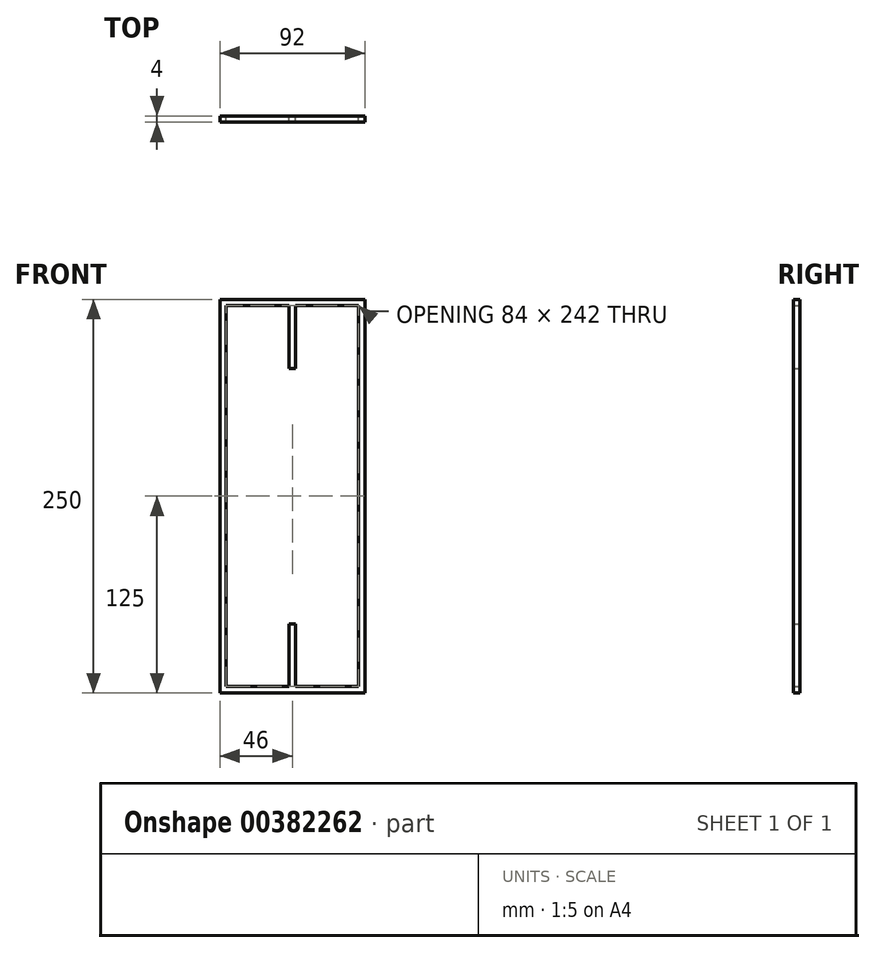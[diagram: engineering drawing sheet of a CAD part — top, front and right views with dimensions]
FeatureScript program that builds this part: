
annotation { "Feature Type Name" : "Feature", "Feature Type Description" : "" }
export const myFeature = defineFeature(function(context is Context, id is Id, definition is map)
    precondition{}
    {
        {
            var Q0;
            Q0=qCreatedBy(makeId("Front.planeOp"),FACE);
            var sketch = newSketch(context, id + "F0", { "sketchPlane" : qUnion([Q0])});
            skPoint(sketch, "E0", {"position": v(0, 0) * mm});
            skPoint(sketch, "E1", {"position": v(46, 0) * mm});
            skPoint(sketch, "E2", {"position": v(0, 125) * mm});
            skPoint(sketch, "E3", {"position": v(-95.35, 0) * mm});
            skLineSegment(sketch, "E4", {"start": v(-95.35, 0) * mm, "end": v(96.76, 0) * mm});
            skPoint(sketch, "E5.MirrorP", {"position": v(0, -125) * mm});
            skLineSegment(sketch, "E6", {"start": v(0, 125) * mm, "end": v(0, -125) * mm});
            skPoint(sketch, "E7", {"position": v(46, 125) * mm});
            skPoint(sketch, "E8.MirrorP", {"position": v(-46, 0) * mm});
            skPoint(sketch, "E9", {"position": v(-46, 125) * mm});
            skPoint(sketch, "E10", {"position": v(46, -125) * mm});
            skPoint(sketch, "E11", {"position": v(-46, -125) * mm});
            skLineSegment(sketch, "E12.bottom", {"start": v(46, 125) * mm, "end": v(42, 125) * mm});
            skLineSegment(sketch, "E12.top", {"start": v(46, -125) * mm, "end": v(42, -125) * mm});
            skLineSegment(sketch, "E12.left", {"start": v(46, 125) * mm, "end": v(46, -125) * mm});
            skLineSegment(sketch, "E12.right", {"start": v(42, 125) * mm, "end": v(42, -125) * mm});
            skLineSegment(sketch, "E13.bottom", {"start": v(-46, 125) * mm, "end": v(-42, 125) * mm});
            skLineSegment(sketch, "E13.top", {"start": v(-46, -125) * mm, "end": v(-42, -125) * mm});
            skLineSegment(sketch, "E13.left", {"start": v(-46, 125) * mm, "end": v(-46, -125) * mm});
            skLineSegment(sketch, "E13.right", {"start": v(-42, 125) * mm, "end": v(-42, -125) * mm});
            skLineSegment(sketch, "E14.bottom", {"start": v(-42, 125) * mm, "end": v(42, 125) * mm});
            skLineSegment(sketch, "E14.top", {"start": v(-42, 121) * mm, "end": v(42, 121) * mm});
            skLineSegment(sketch, "E14.left", {"start": v(-42, 125) * mm, "end": v(-42, 121) * mm});
            skLineSegment(sketch, "E14.right", {"start": v(42, 125) * mm, "end": v(42, 121) * mm});
            skLineSegment(sketch, "E15.bottom", {"start": v(-42, -125) * mm, "end": v(42, -125) * mm});
            skLineSegment(sketch, "E15.top", {"start": v(-42, -121) * mm, "end": v(42, -121) * mm});
            skLineSegment(sketch, "E15.left", {"start": v(-42, -125) * mm, "end": v(-42, -121) * mm});
            skLineSegment(sketch, "E15.right", {"start": v(42, -125) * mm, "end": v(42, -121) * mm});
            skPoint(sketch, "E16", {"position": v(-42, 81) * mm});
            skPoint(sketch, "E17", {"position": v(42, 81) * mm});
            skPoint(sketch, "E18", {"position": v(42, -81) * mm});
            skPoint(sketch, "E19", {"position": v(-42, -81) * mm});
            skPoint(sketch, "E20", {"position": v(42, -15) * mm});
            skPoint(sketch, "E21", {"position": v(-42, -15) * mm});
            skPoint(sketch, "E22", {"position": v(-42, 15) * mm});
            skPoint(sketch, "E23", {"position": v(42, 15) * mm});
            skLineSegment(sketch, "E24.bottom", {"start": v(-42, 15) * mm, "end": v(42, 15) * mm});
            skLineSegment(sketch, "E24.top", {"start": v(-42, -15) * mm, "end": v(42, -15) * mm});
            skLineSegment(sketch, "E24.left", {"start": v(-42, 15) * mm, "end": v(-42, -15) * mm});
            skLineSegment(sketch, "E24.right", {"start": v(42, 15) * mm, "end": v(42, -15) * mm});
            skLineSegment(sketch, "E25.bottom", {"start": v(-42, -81) * mm, "end": v(42, -81) * mm});
            skLineSegment(sketch, "E25.top", {"start": v(-42, -77) * mm, "end": v(42, -77) * mm});
            skLineSegment(sketch, "E25.left", {"start": v(-42, -81) * mm, "end": v(-42, -77) * mm});
            skLineSegment(sketch, "E25.right", {"start": v(42, -81) * mm, "end": v(42, -77) * mm});
            skLineSegment(sketch, "E26.bottom", {"start": v(-42, 81) * mm, "end": v(42, 81) * mm});
            skLineSegment(sketch, "E26.top", {"start": v(-42, 77) * mm, "end": v(42, 77) * mm});
            skLineSegment(sketch, "E26.left", {"start": v(-42, 81) * mm, "end": v(-42, 77) * mm});
            skLineSegment(sketch, "E26.right", {"start": v(42, 81) * mm, "end": v(42, 77) * mm});
            skLineSegment(sketch, "E27.top", {"start": v(-42, 11) * mm, "end": v(42, 11) * mm});
            skLineSegment(sketch, "E27.left", {"start": v(-42, 15) * mm, "end": v(-42, 11) * mm});
            skLineSegment(sketch, "E27.right", {"start": v(42, 15) * mm, "end": v(42, 11) * mm});
            skLineSegment(sketch, "E28.top", {"start": v(-42, -11) * mm, "end": v(42, -11) * mm});
            skLineSegment(sketch, "E28.left", {"start": v(-42, -15) * mm, "end": v(-42, -11) * mm});
            skLineSegment(sketch, "E28.right", {"start": v(42, -15) * mm, "end": v(42, -11) * mm});
            skPoint(sketch, "E29", {"position": v(-42, -89) * mm});
            skPoint(sketch, "E30", {"position": v(-2, -81) * mm});
            skPoint(sketch, "E31", {"position": v(0, -81) * mm});
            skPoint(sketch, "E32.MirrorP", {"position": v(2, -81) * mm});
            skLineSegment(sketch, "E33", {"start": v(-2, -81) * mm, "end": v(-2, -121) * mm});
            skLineSegment(sketch, "E34.MirrorCS", {"start": v(2, -81) * mm, "end": v(2, -121) * mm});
            skPoint(sketch, "E35", {"position": v(-2, -113) * mm});
            skLineSegment(sketch, "E36", {"start": v(-42, -89) * mm, "end": v(-22, -89) * mm});
            skLineSegment(sketch, "E37", {"start": v(-2, -113) * mm, "end": v(-22, -113) * mm});
            skLineSegment(sketch, "E38", {"start": v(-22, -89) * mm, "end": v(-2, -113) * mm});
            skLineSegment(sketch, "E39", {"start": v(-42, -89) * mm, "end": v(-22, -113) * mm});
            skPoint(sketch, "E40", {"position": v(-22, -92.12) * mm});
            skPoint(sketch, "E41", {"position": v(-36.24, -92.78) * mm});
            skPoint(sketch, "E42", {"position": v(-2, 121) * mm});
            skLineSegment(sketch, "E43", {"start": v(-2, 121) * mm, "end": v(-2, 81) * mm});
            skLineSegment(sketch, "E44.MirrorCS", {"start": v(2, 121) * mm, "end": v(2, 81) * mm});
            skPoint(sketch, "E45", {"position": v(0, -15) * mm});
            skPoint(sketch, "E46", {"position": v(0, 15) * mm});
            skLineSegment(sketch, "E47", {"start": v(-42, 77) * mm, "end": v(42, 15) * mm});
            skLineSegment(sketch, "E48", {"start": v(-42, 15) * mm, "end": v(42, 77) * mm});
            skLineSegment(sketch, "E49.bottom", {"start": v(-32.6, 70.06) * mm, "end": v(32.6, 70.06) * mm});
            skLineSegment(sketch, "E49.top", {"start": v(-32.6, 21.94) * mm, "end": v(32.6, 21.94) * mm});
            skLineSegment(sketch, "E49.left", {"start": v(-32.6, 70.06) * mm, "end": v(-32.6, 21.94) * mm});
            skLineSegment(sketch, "E49.right", {"start": v(32.6, 70.06) * mm, "end": v(32.6, 21.94) * mm});
            skPoint(sketch, "E49.middle", {"position": v(0, 46) * mm});
            skLineSegment(sketch, "E50", {"start": v(-42, -15) * mm, "end": v(42, -77) * mm});
            skLineSegment(sketch, "E51", {"start": v(-42, -77) * mm, "end": v(42, -15) * mm});
            skLineSegment(sketch, "E52.bottom", {"start": v(32.5, -22.01) * mm, "end": v(-32.5, -22.01) * mm});
            skLineSegment(sketch, "E52.top", {"start": v(32.5, -69.99) * mm, "end": v(-32.5, -69.99) * mm});
            skLineSegment(sketch, "E52.left", {"start": v(32.5, -22.01) * mm, "end": v(32.5, -69.99) * mm});
            skLineSegment(sketch, "E52.right", {"start": v(-32.5, -22.01) * mm, "end": v(-32.5, -69.99) * mm});
            skPoint(sketch, "E52.middle", {"position": v(0, -46) * mm});
            skPoint(sketch, "E53", {"position": v(0, -77) * mm});
            skPoint(sketch, "E54", {"position": v(0, -69.99) * mm});
            skPoint(sketch, "E55", {"position": v(42, -46) * mm});
            skPoint(sketch, "E55.positionSnap0", {"position": v(32.5, -46) * mm});
            skPoint(sketch, "E56", {"position": v(35, -46) * mm});
            skSolve(sketch);
        }
        {
            var Q0;
            Q0 = qSketchRegion(id + "F0", true);
            var Q1;
            {var subQ0=sQuery(id+"F0.wireOp",EDGE,"E25.left");Q1=makeQuery(id+"F0.imprint","IMPRINT",FACE,{"disambiguationData":[TD([[makeQuery(id+"F0.imprint","IMPRINT",EDGE,{"derivedFrom":subQ0}),-1.0]])]});}
            var Q2;
            {var subQ0=sQuery(id+"F0.wireOp",EDGE,"E25.right");Q2=makeQuery(id+"F0.imprint","IMPRINT",FACE,{"disambiguationData":[TD([[makeQuery(id+"F0.imprint","IMPRINT",EDGE,{"derivedFrom":subQ0}),1.0]])]});}
            var Q3;
            {var subQ1=sQuery(id+"F0.wireOp",EDGE,"E25.bottom");var subQ4=sQuery(id+"F0.wireOp",EDGE,"E6");var subQ5=makeQuery(id+"F0.imprint","INTERSECT",VERTEX,{"derivedFrom":[subQ4,subQ1]});Q3=makeQuery(id+"F0.imprint","IMPRINT",FACE,{"disambiguationData":[TD([[makeQuery(id+"F0.imprint","IMPRINT",EDGE,{"disambiguationData":[TD([[subQ5,-1.0]])],"derivedFrom":subQ4}),-1.0]])]});}
            var Q4;
            {var subQ5=sQuery(id+"F0.wireOp",EDGE,"E34.MirrorCS");Q4=makeQuery(id+"F0.imprint","IMPRINT",FACE,{"disambiguationData":[TD([[makeQuery(id+"F0.imprint","IMPRINT",EDGE,{"derivedFrom":subQ5}),-1.0]])]});}
            var Q5;
            {var subQ5=sQuery(id+"F0.wireOp",EDGE,"E28.left");Q5=makeQuery(id+"F0.imprint","IMPRINT",FACE,{"disambiguationData":[TD([[makeQuery(id+"F0.imprint","IMPRINT",EDGE,{"derivedFrom":subQ5}),-1.0]])]});}
            var Q6;
            {var subQ5=sQuery(id+"F0.wireOp",EDGE,"E28.right");Q6=makeQuery(id+"F0.imprint","IMPRINT",FACE,{"disambiguationData":[TD([[makeQuery(id+"F0.imprint","IMPRINT",EDGE,{"derivedFrom":subQ5}),1.0]])]});}
            var Q7;
            {var subQ5=sQuery(id+"F0.wireOp",EDGE,"E27.right");Q7=makeQuery(id+"F0.imprint","IMPRINT",FACE,{"disambiguationData":[TD([[makeQuery(id+"F0.imprint","IMPRINT",EDGE,{"derivedFrom":subQ5}),-1.0]])]});}
            var Q8;
            {var subQ5=sQuery(id+"F0.wireOp",EDGE,"E27.left");Q8=makeQuery(id+"F0.imprint","IMPRINT",FACE,{"disambiguationData":[TD([[makeQuery(id+"F0.imprint","IMPRINT",EDGE,{"derivedFrom":subQ5}),1.0]])]});}
            var Q9;
            {var subQ0=sQuery(id+"F0.wireOp",EDGE,"E26.left");Q9=makeQuery(id+"F0.imprint","IMPRINT",FACE,{"disambiguationData":[TD([[makeQuery(id+"F0.imprint","IMPRINT",EDGE,{"derivedFrom":subQ0}),1.0]])]});}
            var Q10;
            {var subQ0=sQuery(id+"F0.wireOp",EDGE,"E26.right");Q10=makeQuery(id+"F0.imprint","IMPRINT",FACE,{"disambiguationData":[TD([[makeQuery(id+"F0.imprint","IMPRINT",EDGE,{"derivedFrom":subQ0}),-1.0]])]});}
            var Q11;
            {var subQ5=sQuery(id+"F0.wireOp",EDGE,"E44.MirrorCS");Q11=makeQuery(id+"F0.imprint","IMPRINT",FACE,{"disambiguationData":[TD([[makeQuery(id+"F0.imprint","IMPRINT",EDGE,{"derivedFrom":subQ5}),-1.0]])]});}
            var Q12;
            {var subQ5=sQuery(id+"F0.wireOp",EDGE,"E43");Q12=makeQuery(id+"F0.imprint","IMPRINT",FACE,{"disambiguationData":[TD([[makeQuery(id+"F0.imprint","IMPRINT",EDGE,{"derivedFrom":subQ5}),1.0]])]});}
            extrude(context, id + "F1", {"entities" : qUnion([Q0, Q1, Q2, Q3, Q4, Q5, Q6, Q7, Q8, Q9, Q10, Q11, Q12]), "depth" : 4 * mm});
        }
    });
